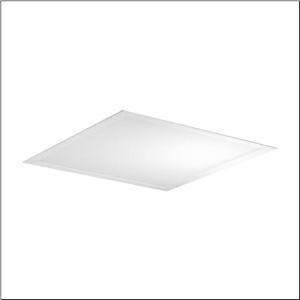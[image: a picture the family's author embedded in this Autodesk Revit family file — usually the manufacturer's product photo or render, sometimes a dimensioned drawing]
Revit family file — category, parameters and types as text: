
# Revit family: apollon_r__21_square_51mq11wd2614_d913
name_source: partatom
category: Lighting Fixtures
units: mm (PartAtom-declared; Revit-internal decimal feet)

## family parameters
Cut with Voids When Loaded = No
Host = Face
Light Source = No
Part Type = Normal
Room Calculation Point = No
Round Connector Dimension = Use Diameter
Shared = No

## types (1)
- Apollon® 21 square (1 x LED, 4150 lm, 24.7 W, 6500K)
    Apparent Load = 25 VA
    CIE Flux Codes = 60 87 97 100 100
    Color Rendering = 80
    Color Temperature = 6500K
    Default Elevation = 1800 mm
    Description = Apollon® 21 square, office luminaire, primary optical cover: micro prismatic cover, of PMMA, CAT 2 (L<= 3000cd/m²), light emission: direct distribution, primary light characteristic: symmetric, installation type: lay-in mounting, LED, rated luminous flux: 4.150lm, luminous efficacy: 168lm/W, light colour: 865, colour temperature: 6500K, with terminal, 5-pole, mains connection: 220..240V, AC/DC, 0/50..60Hz, rated input power: 24.7W, housing, of aluminium, coated, traffic white (RAL 9016), module: M625, length: 620mm, width: 620mm, height: 30mm, housing upper side, of sheet steel, galvanised, protection rating (complete): IP20, protection rating (lamp compartment, on room side): IP50, insulation class (complete): insulation class II (safety insulation), certification: CE, ENEC, impact resistance: IK03, permissible operating ambient temperature: -20..+45°C, permissible storage temperature: -40..+80°C, packaging unit: 1 piece
    Height = 0 mm  [stored 0 ft]
    Lamp = 1 x LED
    Lamp Light Flux = 4150 lm
    Lamp Power = 24.7 W
    Lamp count = 1
    Length = 620 mm
    Luminous efficacy = 168 lm/W
    Manufacturer = Siteco
    ModVariant = No
    Model = 51MQ11WD2614
    Mounting Place = Ceiling
    Mounting Type = Recessed
    Number of Poles = 1
    OnlyDefault = Yes
    Power Factor = 1
    Product Name = Apollon® 21 square
    Product group = office luminaire | ceiling recessed
    ProductGroupID = 401
    Protection Class = Protection class II
    Protection Degree = IP 20
    RLX_Detail_Level = 1
    RLX_Emergency_Light_Flux = 0 lm
    RLX_Emergency_Type = 0
    RLX_Emergency_Type_DB = No
    RlxData = <blob elided: 12937 chars, md5=2f5571df>
    Socket = socket
    Standby Power = 0 W
    System Light Flux = 4150 lm
    System Power = 25 W
    Type Comments = Product without accessories
    Type Image = l_1291054.jpg
    URL = http://relux.com
    VarID = ---
    Voltage = 0 V
    Weight = 0.00 kg
    Width = 620 mm

note: [stored X ft] marks values corroborated as IEEE doubles in the binary element streams (Revit-internal decimal feet)

## geometry (parser evidence)
native form markers: Sweep x12
no freeform markers — native parametric forms only
